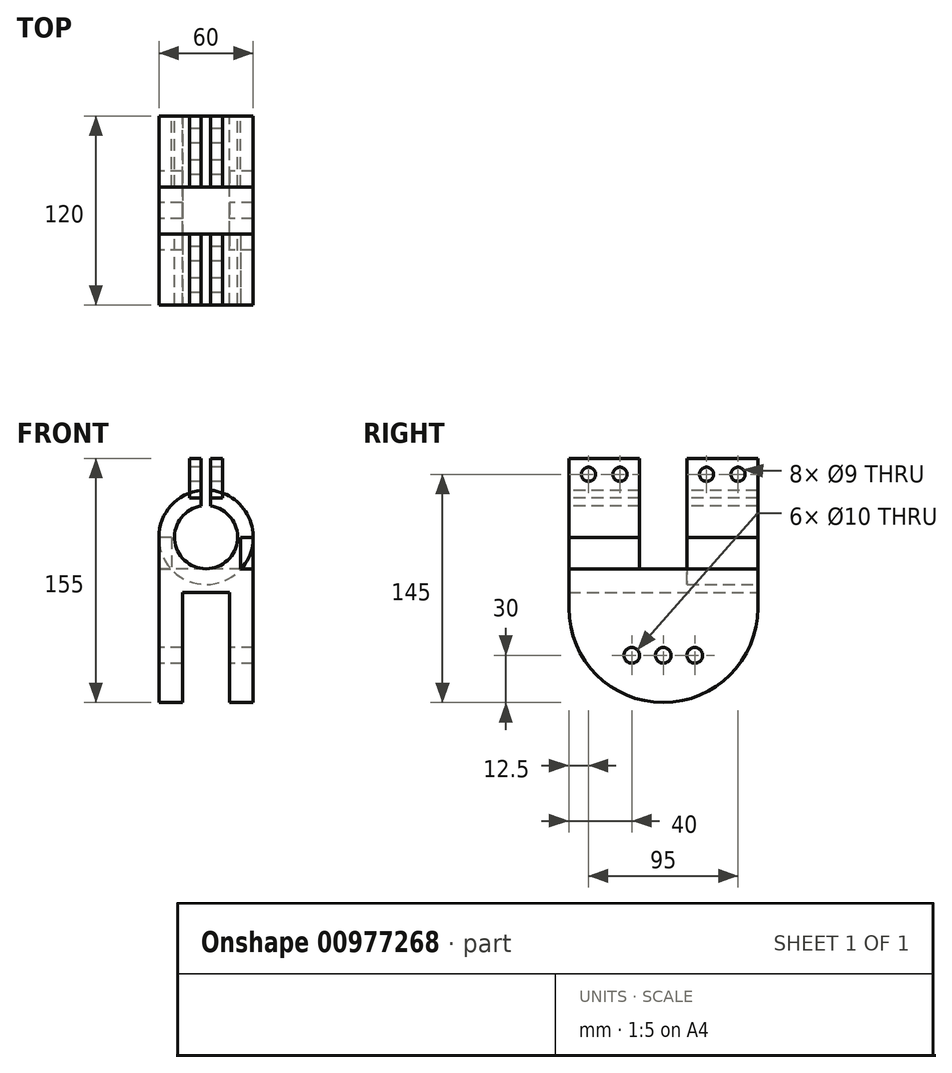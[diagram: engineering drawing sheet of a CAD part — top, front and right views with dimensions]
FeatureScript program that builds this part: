
annotation { "Feature Type Name" : "Feature", "Feature Type Description" : "" }
export const myFeature = defineFeature(function(context is Context, id is Id, definition is map)
    precondition{}
    {
        {
            var Q0;
            Q0=qCreatedBy(makeId("Front.planeOp"),FACE);
            var sketch = newSketch(context, id + "F0", { "sketchPlane" : qUnion([Q0])});
            skCircle(sketch, "E0", {"center": v(0, 0) * mm, "radius": 20 * mm});
            skCircle(sketch, "E1", {"center": v(0, 0) * mm, "radius": 30 * mm});
            skSolve(sketch);
        }
        {
            var Q0;
            Q0=makeQuery(id+"F0.imprint","IMPRINT",FACE,{"disambiguationData":[TD([[makeQuery(id+"F0.imprint","IMPRINT",EDGE,{"derivedFrom":sQuery(id+"F0.wireOp",EDGE,"E0")}),-1.0]])]});
            extrude(context, id + "F1", {"entities" : qUnion([Q0]), "depth" : 120 * mm, "offsetDistance" : 25 * mm});
        }
        {
            var Q0;
            Q0=makeQuery(id+"F0.imprint","IMPRINT",FACE,{"disambiguationData":[TD([[makeQuery(id+"F0.imprint","IMPRINT",EDGE,{"derivedFrom":sQuery(id+"F0.wireOp",EDGE,"E0")}),-1.0]])]});
            extrude(context, id + "F2", {"entities" : qUnion([Q0]), "operationType" : NewBodyOperationType.ADD, "depth" : 120 * mm, "offsetDistance" : 25 * mm});
        }
        {
            var Q0;
            Q0=makeQuery(id+"F1.opExtrude","CAP_FACE",FACE,{"disambiguationData":[OSD([sQuery(id+"F0.wireOp",EDGE,"E0"),sQuery(id+"F0.wireOp",EDGE,"E1")])],"isStart":false});
            var sketch = newSketch(context, id + "F3", { "sketchPlane" : qUnion([Q0])});
            skLineSegment(sketch, "E2.bottom", {"start": v(-3, 32) * mm, "end": v(3, 32) * mm});
            skLineSegment(sketch, "E2.top", {"start": v(-3, 18) * mm, "end": v(3, 18) * mm});
            skLineSegment(sketch, "E2.left", {"start": v(-3, 32) * mm, "end": v(-3, 18) * mm});
            skLineSegment(sketch, "E2.right", {"start": v(3, 32) * mm, "end": v(3, 18) * mm});
            skSolve(sketch);
        }
        {
            var Q0;
            {var subQ0=sQuery(id+"F3.wireOp",EDGE,"E2.left");var subQ1=makeQuery(id+"F1.opExtrude","CAP_EDGE",EDGE,{"disambiguationData":[OSD([sQuery(id+"F0.wireOp",EDGE,"E1")])],"isStart":false});var subQ2=makeQuery(id+"F3.imprint","INTERSECT",VERTEX,{"derivedFrom":[subQ1,subQ0]});Q0=makeQuery(id+"F3.imprint","IMPRINT",FACE,{"disambiguationData":[TD([[makeQuery(id+"F3.imprint","IMPRINT",EDGE,{"disambiguationData":[TD([[subQ2,-1.0]])],"derivedFrom":subQ0}),1.0]])]});}
            extrude(context, id + "F4", {"entities" : qUnion([Q0]), "operationType" : NewBodyOperationType.REMOVE, "oppositeDirection" : true, "depth" : 120 * mm, "offsetDistance" : 25 * mm});
        }
        {
            var Q0;
            Q0=qCreatedBy(makeId("Top.planeOp"),FACE);
            var sketch = newSketch(context, id + "F5", { "sketchPlane" : qUnion([Q0])});
            skLineSegment(sketch, "E3.bottom", {"start": v(-60, -45) * mm, "end": v(60, -45) * mm});
            skLineSegment(sketch, "E3.top", {"start": v(-60, -75) * mm, "end": v(60, -75) * mm});
            skLineSegment(sketch, "E3.left", {"start": v(-60, -45) * mm, "end": v(-60, -75) * mm});
            skLineSegment(sketch, "E3.right", {"start": v(60, -45) * mm, "end": v(60, -75) * mm});
            skSolve(sketch);
        }
        {
            var Q0;
            Q0=makeQuery(id+"F5.imprint","IMPRINT",FACE,{"disambiguationData":[TD([[makeQuery(id+"F5.imprint","IMPRINT",EDGE,{"derivedFrom":sQuery(id+"F5.wireOp",EDGE,"E3.bottom")}),-1.0]])]});
            extrude(context, id + "F6", {"entities" : qUnion([Q0]), "operationType" : NewBodyOperationType.REMOVE, "oppositeDirection" : true, "depth" : 100 * mm, "offsetDistance" : 25 * mm});
        }
        {
            var Q0;
            Q0=qCreatedBy(makeId("Top.planeOp"),FACE);
            var sketch = newSketch(context, id + "F7", { "sketchPlane" : qUnion([Q0])});
            skLineSegment(sketch, "E4.bottom", {"start": v(-60, -75) * mm, "end": v(60, -75) * mm});
            skLineSegment(sketch, "E4.top", {"start": v(-60, -45) * mm, "end": v(60, -45) * mm});
            skLineSegment(sketch, "E4.left", {"start": v(-60, -75) * mm, "end": v(-60, -45) * mm});
            skLineSegment(sketch, "E4.right", {"start": v(60, -75) * mm, "end": v(60, -45) * mm});
            skSolve(sketch);
        }
        {
            var Q0;
            Q0=makeQuery(id+"F7.imprint","IMPRINT",FACE,{"disambiguationData":[TD([[makeQuery(id+"F7.imprint","IMPRINT",EDGE,{"derivedFrom":sQuery(id+"F7.wireOp",EDGE,"E4.bottom")}),1.0]])]});
            extrude(context, id + "F8", {"entities" : qUnion([Q0]), "operationType" : NewBodyOperationType.REMOVE, "oppositeDirection" : true, "depth" : 100 * mm, "offsetDistance" : 25 * mm, "symmetric" : true});
        }
        {
            var Q0;
            Q0=qCreatedBy(makeId("Top.planeOp"),FACE);
            cPlane(context, id + "F9", {"entities" : qUnion([Q0]), "cplaneType" : CPlaneType.OFFSET, "offset" : 25 * mm, "width" : 150 * mm, "height" : 150 * mm});
        }
        {
            var Q0;
            Q0=qCreatedBy(id+"F9.planeOp",FACE);
            var sketch = newSketch(context, id + "F10", { "sketchPlane" : qUnion([Q0])});
            skLineSegment(sketch, "E5.bottom", {"start": v(-10.5, 0) * mm, "end": v(-3, 0) * mm});
            skLineSegment(sketch, "E5.top", {"start": v(-10.5, -45) * mm, "end": v(-3, -45) * mm});
            skLineSegment(sketch, "E5.left", {"start": v(-10.5, 0) * mm, "end": v(-10.5, -45) * mm});
            skLineSegment(sketch, "E5.right", {"start": v(-3, 0) * mm, "end": v(-3, -45) * mm});
            skLineSegment(sketch, "E6.bottom", {"start": v(3, 0) * mm, "end": v(10.5, 0) * mm});
            skLineSegment(sketch, "E6.top", {"start": v(3, -45) * mm, "end": v(10.5, -45) * mm});
            skLineSegment(sketch, "E6.left", {"start": v(3, 0) * mm, "end": v(3, -45) * mm});
            skLineSegment(sketch, "E6.right", {"start": v(10.5, 0) * mm, "end": v(10.5, -45) * mm});
            skLineSegment(sketch, "E7.bottom", {"start": v(-10.5, -75) * mm, "end": v(-3, -75) * mm});
            skLineSegment(sketch, "E7.top", {"start": v(-10.5, -120) * mm, "end": v(-3, -120) * mm});
            skLineSegment(sketch, "E7.left", {"start": v(-10.5, -75) * mm, "end": v(-10.5, -120) * mm});
            skLineSegment(sketch, "E7.right", {"start": v(-3, -75) * mm, "end": v(-3, -120) * mm});
            skLineSegment(sketch, "E8.bottom", {"start": v(3, -75) * mm, "end": v(10.5, -75) * mm});
            skLineSegment(sketch, "E8.top", {"start": v(3, -120) * mm, "end": v(10.5, -120) * mm});
            skLineSegment(sketch, "E8.left", {"start": v(3, -75) * mm, "end": v(3, -120) * mm});
            skLineSegment(sketch, "E8.right", {"start": v(10.5, -75) * mm, "end": v(10.5, -120) * mm});
            skSolve(sketch);
        }
        {
            var Q0;
            Q0=makeQuery(id+"F10.imprint","IMPRINT",FACE,{"disambiguationData":[TD([[makeQuery(id+"F10.imprint","IMPRINT",EDGE,{"derivedFrom":sQuery(id+"F10.wireOp",EDGE,"E6.bottom")}),-1.0]])]});
            extrude(context, id + "F11", {"entities" : qUnion([Q0]), "depth" : 25 * mm, "offsetDistance" : 25 * mm});
        }
        {
            var Q0;
            Q0=makeQuery(id+"F10.imprint","IMPRINT",FACE,{"disambiguationData":[TD([[makeQuery(id+"F10.imprint","IMPRINT",EDGE,{"derivedFrom":sQuery(id+"F10.wireOp",EDGE,"E5.bottom")}),-1.0]])]});
            extrude(context, id + "F12", {"entities" : qUnion([Q0]), "depth" : 25 * mm, "offsetDistance" : 25 * mm});
        }
        {
            var Q0;
            Q0=makeQuery(id+"F10.imprint","IMPRINT",FACE,{"disambiguationData":[TD([[makeQuery(id+"F10.imprint","IMPRINT",EDGE,{"derivedFrom":sQuery(id+"F10.wireOp",EDGE,"E7.bottom")}),-1.0]])]});
            extrude(context, id + "F13", {"entities" : qUnion([Q0]), "depth" : 25 * mm, "offsetDistance" : 25 * mm});
        }
        {
            var Q0;
            Q0=makeQuery(id+"F10.imprint","IMPRINT",FACE,{"disambiguationData":[TD([[makeQuery(id+"F10.imprint","IMPRINT",EDGE,{"derivedFrom":sQuery(id+"F10.wireOp",EDGE,"E8.bottom")}),-1.0]])]});
            extrude(context, id + "F14", {"entities" : qUnion([Q0]), "depth" : 25 * mm, "offsetDistance" : 25 * mm});
        }
        {
            var Q0;
            Q0=makeQuery(id+"F13.opExtrude","SWEPT_FACE",FACE,{"disambiguationData":[OSD([sQuery(id+"F10.wireOp",EDGE,"E7.left")])]});
            var sketch = newSketch(context, id + "F15", { "sketchPlane" : qUnion([Q0])});
            skCircle(sketch, "E9", {"center": v(87.5, 40) * mm, "radius": 4.5 * mm});
            skCircle(sketch, "E10", {"center": v(107.5, 40) * mm, "radius": 4.5 * mm});
            skSolve(sketch);
        }
        {
            var Q0;
            Q0=makeQuery(id+"F15.imprint","IMPRINT",FACE,{"disambiguationData":[TD([[makeQuery(id+"F15.imprint","IMPRINT",EDGE,{"derivedFrom":sQuery(id+"F15.wireOp",EDGE,"E10")}),1.0]])]});
            var Q1;
            Q1=makeQuery(id+"F15.imprint","IMPRINT",FACE,{"disambiguationData":[TD([[makeQuery(id+"F15.imprint","IMPRINT",EDGE,{"derivedFrom":sQuery(id+"F15.wireOp",EDGE,"E9")}),1.0]])]});
            extrude(context, id + "F16", {"entities" : qUnion([Q0, Q1]), "operationType" : NewBodyOperationType.REMOVE, "oppositeDirection" : true, "depth" : 100 * mm, "offsetDistance" : 25 * mm, "symmetric" : true});
        }
        {
            var Q0;
            Q0=makeQuery(id+"F14.opExtrude","SWEPT_FACE",FACE,{"disambiguationData":[OSD([sQuery(id+"F10.wireOp",EDGE,"E8.right")])]});
            var sketch = newSketch(context, id + "F17", { "sketchPlane" : qUnion([Q0])});
            skCircle(sketch, "E11", {"center": v(-107.5, 40) * mm, "radius": 4.5 * mm});
            skCircle(sketch, "E12", {"center": v(-87.5, 40) * mm, "radius": 4.5 * mm});
            skSolve(sketch);
        }
        {
            var Q0;
            Q0=makeQuery(id+"F17.imprint","IMPRINT",FACE,{"disambiguationData":[TD([[makeQuery(id+"F17.imprint","IMPRINT",EDGE,{"derivedFrom":sQuery(id+"F17.wireOp",EDGE,"E11")}),1.0]])]});
            extrude(context, id + "F18", {"entities" : qUnion([Q0]), "operationType" : NewBodyOperationType.REMOVE, "oppositeDirection" : true, "depth" : 100 * mm, "offsetDistance" : 25 * mm, "symmetric" : true});
        }
        {
            var Q0;
            Q0=makeQuery(id+"F17.imprint","IMPRINT",FACE,{"disambiguationData":[TD([[makeQuery(id+"F17.imprint","IMPRINT",EDGE,{"derivedFrom":sQuery(id+"F17.wireOp",EDGE,"E12")}),1.0]])]});
            extrude(context, id + "F19", {"entities" : qUnion([Q0]), "operationType" : NewBodyOperationType.REMOVE, "oppositeDirection" : true, "depth" : 100 * mm, "offsetDistance" : 25 * mm, "symmetric" : true});
        }
        {
            var Q0;
            Q0=makeQuery(id+"F12.opExtrude","SWEPT_FACE",FACE,{"disambiguationData":[OSD([sQuery(id+"F10.wireOp",EDGE,"E5.left")])]});
            var sketch = newSketch(context, id + "F20", { "sketchPlane" : qUnion([Q0])});
            skCircle(sketch, "E13", {"center": v(12.5, 40) * mm, "radius": 4.5 * mm});
            skCircle(sketch, "E14", {"center": v(32.5, 40) * mm, "radius": 4.5 * mm});
            skSolve(sketch);
        }
        {
            var Q0;
            Q0=makeQuery(id+"F20.imprint","IMPRINT",FACE,{"disambiguationData":[TD([[makeQuery(id+"F20.imprint","IMPRINT",EDGE,{"derivedFrom":sQuery(id+"F20.wireOp",EDGE,"E13")}),1.0]])]});
            extrude(context, id + "F21", {"entities" : qUnion([Q0]), "operationType" : NewBodyOperationType.REMOVE, "oppositeDirection" : true, "depth" : 100 * mm, "offsetDistance" : 25 * mm});
        }
        {
            var Q0;
            Q0=makeQuery(id+"F20.imprint","IMPRINT",FACE,{"disambiguationData":[TD([[makeQuery(id+"F20.imprint","IMPRINT",EDGE,{"derivedFrom":sQuery(id+"F20.wireOp",EDGE,"E14")}),1.0]])]});
            extrude(context, id + "F22", {"entities" : qUnion([Q0]), "operationType" : NewBodyOperationType.REMOVE, "oppositeDirection" : true, "depth" : 100 * mm, "offsetDistance" : 25 * mm, "symmetric" : true});
        }
        {
            var Q0;
            Q0=makeQuery(id+"F11.opExtrude","SWEPT_FACE",FACE,{"disambiguationData":[OSD([sQuery(id+"F10.wireOp",EDGE,"E6.right")])]});
            var sketch = newSketch(context, id + "F23", { "sketchPlane" : qUnion([Q0])});
            skCircle(sketch, "E15", {"center": v(-32.5, 40) * mm, "radius": 4.5 * mm});
            skCircle(sketch, "E16", {"center": v(-12.5, 40) * mm, "radius": 4.5 * mm});
            skSolve(sketch);
        }
        {
            var Q0;
            Q0=makeQuery(id+"F23.imprint","IMPRINT",FACE,{"disambiguationData":[TD([[makeQuery(id+"F23.imprint","IMPRINT",EDGE,{"derivedFrom":sQuery(id+"F23.wireOp",EDGE,"E15")}),1.0]])]});
            extrude(context, id + "F24", {"entities" : qUnion([Q0]), "operationType" : NewBodyOperationType.REMOVE, "oppositeDirection" : true, "depth" : 100 * mm, "offsetDistance" : 25 * mm, "symmetric" : true});
        }
        {
            var Q0;
            Q0=makeQuery(id+"F23.imprint","IMPRINT",FACE,{"disambiguationData":[TD([[makeQuery(id+"F23.imprint","IMPRINT",EDGE,{"derivedFrom":sQuery(id+"F23.wireOp",EDGE,"E16")}),1.0]])]});
            extrude(context, id + "F25", {"entities" : qUnion([Q0]), "operationType" : NewBodyOperationType.REMOVE, "oppositeDirection" : true, "depth" : 100 * mm, "offsetDistance" : 25 * mm});
        }
        {
            var Q0;
            Q0=qCreatedBy(makeId("Top.planeOp"),FACE);
            cPlane(context, id + "F26", {"entities" : qUnion([Q0]), "cplaneType" : CPlaneType.OFFSET, "offset" : 20 * mm, "oppositeDirection" : true, "width" : 150 * mm, "height" : 150 * mm});
        }
        {
            var Q0;
            Q0=qCreatedBy(id+"F26.planeOp",FACE);
            var sketch = newSketch(context, id + "F27", { "sketchPlane" : qUnion([Q0])});
            skLineSegment(sketch, "E17.bottom", {"start": v(-30, -120) * mm, "end": v(30, -120) * mm});
            skLineSegment(sketch, "E17.top", {"start": v(-30, 0) * mm, "end": v(30, 0) * mm});
            skLineSegment(sketch, "E17.left", {"start": v(-30, -120) * mm, "end": v(-30, 0) * mm});
            skLineSegment(sketch, "E17.right", {"start": v(30, -120) * mm, "end": v(30, 0) * mm});
            skSolve(sketch);
        }
        {
            var Q0;
            Q0=makeQuery(id+"F27.imprint","IMPRINT",FACE,{"disambiguationData":[TD([[makeQuery(id+"F27.imprint","IMPRINT",EDGE,{"derivedFrom":sQuery(id+"F27.wireOp",EDGE,"E17.bottom")}),1.0]])]});
            extrude(context, id + "F28", {"entities" : qUnion([Q0]), "oppositeDirection" : true, "depth" : 25 * mm, "offsetDistance" : 25 * mm});
        }
        {
            var Q0;
            Q0=makeQuery(id+"F28.opExtrude","SWEPT_FACE",FACE,{"disambiguationData":[OSD([sQuery(id+"F27.wireOp",EDGE,"E17.right")])]});
            var sketch = newSketch(context, id + "F29", { "sketchPlane" : qUnion([Q0])});
            skArc(sketch, "E18", {"start": v(-120, -45) * mm, "mid": v(-60, -105) * mm, "end": v(0, -45) * mm});
            skSolve(sketch);
        }
        {
            var Q0;
            Q0=makeQuery(id+"F29.imprint","IMPRINT",FACE,{"disambiguationData":[TD([[makeQuery(id+"F29.imprint","IMPRINT",EDGE,{"derivedFrom":sQuery(id+"F29.wireOp",EDGE,"E18")}),1.0]])]});
            extrude(context, id + "F30", {"entities" : qUnion([Q0]), "operationType" : NewBodyOperationType.ADD, "oppositeDirection" : true, "depth" : 15 * mm, "offsetDistance" : 25 * mm});
        }
        {
            var Q0;
            Q0=makeQuery(id+"F28.opExtrude","SWEPT_FACE",FACE,{"disambiguationData":[OSD([sQuery(id+"F27.wireOp",EDGE,"E17.left")])]});
            var sketch = newSketch(context, id + "F31", { "sketchPlane" : qUnion([Q0])});
            skArc(sketch, "E19", {"start": v(0, -45) * mm, "mid": v(60, -105) * mm, "end": v(120, -45) * mm});
            skSolve(sketch);
        }
        {
            var Q0;
            Q0=makeQuery(id+"F31.imprint","IMPRINT",FACE,{"disambiguationData":[TD([[makeQuery(id+"F31.imprint","IMPRINT",EDGE,{"derivedFrom":sQuery(id+"F31.wireOp",EDGE,"E19")}),1.0]])]});
            extrude(context, id + "F32", {"entities" : qUnion([Q0]), "operationType" : NewBodyOperationType.ADD, "oppositeDirection" : true, "depth" : 15 * mm, "offsetDistance" : 25 * mm});
        }
        {
            var Q0;
            {var subQ0=sQuery(id+"F27.wireOp",EDGE,"E17.left");Q0=makeQuery(id+"F32.boolean.opBoolean","MERGE",FACE,{"derivedFrom":[makeQuery(id+"F28.opExtrude","SWEPT_FACE",FACE,{"disambiguationData":[OSD([subQ0])]}),makeQuery(id+"F32.opExtrude","CAP_FACE",FACE,{"disambiguationData":[OSD([subQ0,sQuery(id+"F31.wireOp",EDGE,"E19")])],"isStart":true})]});}
            var sketch = newSketch(context, id + "F33", { "sketchPlane" : qUnion([Q0])});
            skCircle(sketch, "E20", {"center": v(60, -75) * mm, "radius": 5 * mm});
            skCircle(sketch, "E21", {"center": v(40, -75) * mm, "radius": 5 * mm});
            skCircle(sketch, "E22", {"center": v(80, -75) * mm, "radius": 5 * mm});
            skSolve(sketch);
        }
        {
            var Q0;
            Q0=makeQuery(id+"F33.imprint","IMPRINT",FACE,{"disambiguationData":[TD([[makeQuery(id+"F33.imprint","IMPRINT",EDGE,{"derivedFrom":sQuery(id+"F33.wireOp",EDGE,"E21")}),1.0]])]});
            extrude(context, id + "F34", {"entities" : qUnion([Q0]), "operationType" : NewBodyOperationType.REMOVE, "endBound" : BoundingType.THROUGH_ALL, "oppositeDirection" : true, "depth" : 25 * mm, "offsetDistance" : 25 * mm});
        }
        {
            var Q0;
            Q0=makeQuery(id+"F33.imprint","IMPRINT",FACE,{"disambiguationData":[TD([[makeQuery(id+"F33.imprint","IMPRINT",EDGE,{"derivedFrom":sQuery(id+"F33.wireOp",EDGE,"E20")}),1.0]])]});
            extrude(context, id + "F35", {"entities" : qUnion([Q0]), "operationType" : NewBodyOperationType.REMOVE, "endBound" : BoundingType.THROUGH_ALL, "oppositeDirection" : true, "depth" : 25 * mm, "offsetDistance" : 25 * mm});
        }
        {
            var Q0;
            Q0=makeQuery(id+"F33.imprint","IMPRINT",FACE,{"disambiguationData":[TD([[makeQuery(id+"F33.imprint","IMPRINT",EDGE,{"derivedFrom":sQuery(id+"F33.wireOp",EDGE,"E22")}),1.0]])]});
            extrude(context, id + "F36", {"entities" : qUnion([Q0]), "operationType" : NewBodyOperationType.REMOVE, "endBound" : BoundingType.THROUGH_ALL, "oppositeDirection" : true, "depth" : 25 * mm, "offsetDistance" : 25 * mm});
        }
        {
            var Q0;
            Q0=makeQuery(id+"F28.opExtrude","SWEPT_FACE",FACE,{"disambiguationData":[OSD([sQuery(id+"F27.wireOp",EDGE,"E17.top")])]});
            var sketch = newSketch(context, id + "F37", { "sketchPlane" : qUnion([Q0])});
            skLineSegment(sketch, "E23.bottom", {"start": v(-15, -45) * mm, "end": v(15, -45) * mm});
            skLineSegment(sketch, "E23.top", {"start": v(-15, -35) * mm, "end": v(15, -35) * mm});
            skLineSegment(sketch, "E23.left", {"start": v(-15, -45) * mm, "end": v(-15, -35) * mm});
            skLineSegment(sketch, "E23.right", {"start": v(15, -45) * mm, "end": v(15, -35) * mm});
            skSolve(sketch);
        }
        {
            var Q0;
            Q0=makeQuery(id+"F37.imprint","IMPRINT",FACE,{"disambiguationData":[TD([[makeQuery(id+"F37.imprint","IMPRINT",EDGE,{"derivedFrom":sQuery(id+"F37.wireOp",EDGE,"E23.bottom")}),-1.0]])]});
            extrude(context, id + "F38", {"entities" : qUnion([Q0]), "operationType" : NewBodyOperationType.REMOVE, "endBound" : BoundingType.THROUGH_ALL, "oppositeDirection" : true, "depth" : 25 * mm, "offsetDistance" : 25 * mm});
        }
        {
            var Q0;
            Q0=makeQuery(id+"F28.opExtrude","SWEPT_FACE",FACE,{"disambiguationData":[OSD([sQuery(id+"F27.wireOp",EDGE,"E17.top")])]});
            var sketch = newSketch(context, id + "F39", { "sketchPlane" : qUnion([Q0])});
            skLineSegment(sketch, "E24.bottom", {"start": v(22, 0) * mm, "end": v(30, 0) * mm});
            skLineSegment(sketch, "E24.top", {"start": v(22, -20) * mm, "end": v(30, -20) * mm});
            skLineSegment(sketch, "E24.left", {"start": v(22, 0) * mm, "end": v(22, -20) * mm});
            skLineSegment(sketch, "E24.right", {"start": v(30, 0) * mm, "end": v(30, -20) * mm});
            skLineSegment(sketch, "E25.bottom", {"start": v(-30, 0) * mm, "end": v(-22, 0) * mm});
            skLineSegment(sketch, "E25.top", {"start": v(-30, -20) * mm, "end": v(-22, -20) * mm});
            skLineSegment(sketch, "E25.left", {"start": v(-30, 0) * mm, "end": v(-30, -20) * mm});
            skLineSegment(sketch, "E25.right", {"start": v(-22, 0) * mm, "end": v(-22, -20) * mm});
            skSolve(sketch);
        }
        {
            var Q0;
            Q0=makeQuery(id+"F39.imprint","IMPRINT",FACE,{"disambiguationData":[TD([[makeQuery(id+"F39.imprint","IMPRINT",EDGE,{"derivedFrom":sQuery(id+"F39.wireOp",EDGE,"E25.bottom")}),-1.0]])]});
            extrude(context, id + "F40", {"entities" : qUnion([Q0]), "oppositeDirection" : true, "depth" : 45 * mm, "offsetDistance" : 25 * mm});
        }
        {
            var Q0;
            Q0=makeQuery(id+"F39.imprint","IMPRINT",FACE,{"disambiguationData":[TD([[makeQuery(id+"F39.imprint","IMPRINT",EDGE,{"derivedFrom":sQuery(id+"F39.wireOp",EDGE,"E24.bottom")}),-1.0]])]});
            extrude(context, id + "F41", {"entities" : qUnion([Q0]), "oppositeDirection" : true, "depth" : 45 * mm, "offsetDistance" : 25 * mm});
        }
        {
            var Q0;
            Q0=makeQuery(id+"F28.opExtrude","SWEPT_FACE",FACE,{"disambiguationData":[OSD([sQuery(id+"F27.wireOp",EDGE,"E17.bottom")])]});
            var sketch = newSketch(context, id + "F42", { "sketchPlane" : qUnion([Q0])});
            skLineSegment(sketch, "E26.bottom", {"start": v(-30, 0) * mm, "end": v(-22, 0) * mm});
            skLineSegment(sketch, "E26.top", {"start": v(-30, -20) * mm, "end": v(-22, -20) * mm});
            skLineSegment(sketch, "E26.left", {"start": v(-30, 0) * mm, "end": v(-30, -20) * mm});
            skLineSegment(sketch, "E26.right", {"start": v(-22, 0) * mm, "end": v(-22, -20) * mm});
            skLineSegment(sketch, "E27.bottom", {"start": v(22, 0) * mm, "end": v(30, 0) * mm});
            skLineSegment(sketch, "E27.top", {"start": v(22, -20) * mm, "end": v(30, -20) * mm});
            skLineSegment(sketch, "E27.left", {"start": v(22, 0) * mm, "end": v(22, -20) * mm});
            skLineSegment(sketch, "E27.right", {"start": v(30, 0) * mm, "end": v(30, -20) * mm});
            skSolve(sketch);
        }
        {
            var Q0;
            Q0=makeQuery(id+"F42.imprint","IMPRINT",FACE,{"disambiguationData":[TD([[makeQuery(id+"F42.imprint","IMPRINT",EDGE,{"derivedFrom":sQuery(id+"F42.wireOp",EDGE,"E26.bottom")}),-1.0]])]});
            extrude(context, id + "F43", {"entities" : qUnion([Q0]), "operationType" : NewBodyOperationType.ADD, "oppositeDirection" : true, "depth" : 45 * mm, "offsetDistance" : 25 * mm});
        }
        {
            var Q0;
            Q0=makeQuery(id+"F42.imprint","IMPRINT",FACE,{"disambiguationData":[TD([[makeQuery(id+"F42.imprint","IMPRINT",EDGE,{"derivedFrom":sQuery(id+"F42.wireOp",EDGE,"E27.bottom")}),-1.0]])]});
            extrude(context, id + "F44", {"entities" : qUnion([Q0]), "oppositeDirection" : true, "depth" : 45 * mm, "offsetDistance" : 25 * mm});
        }
    });
